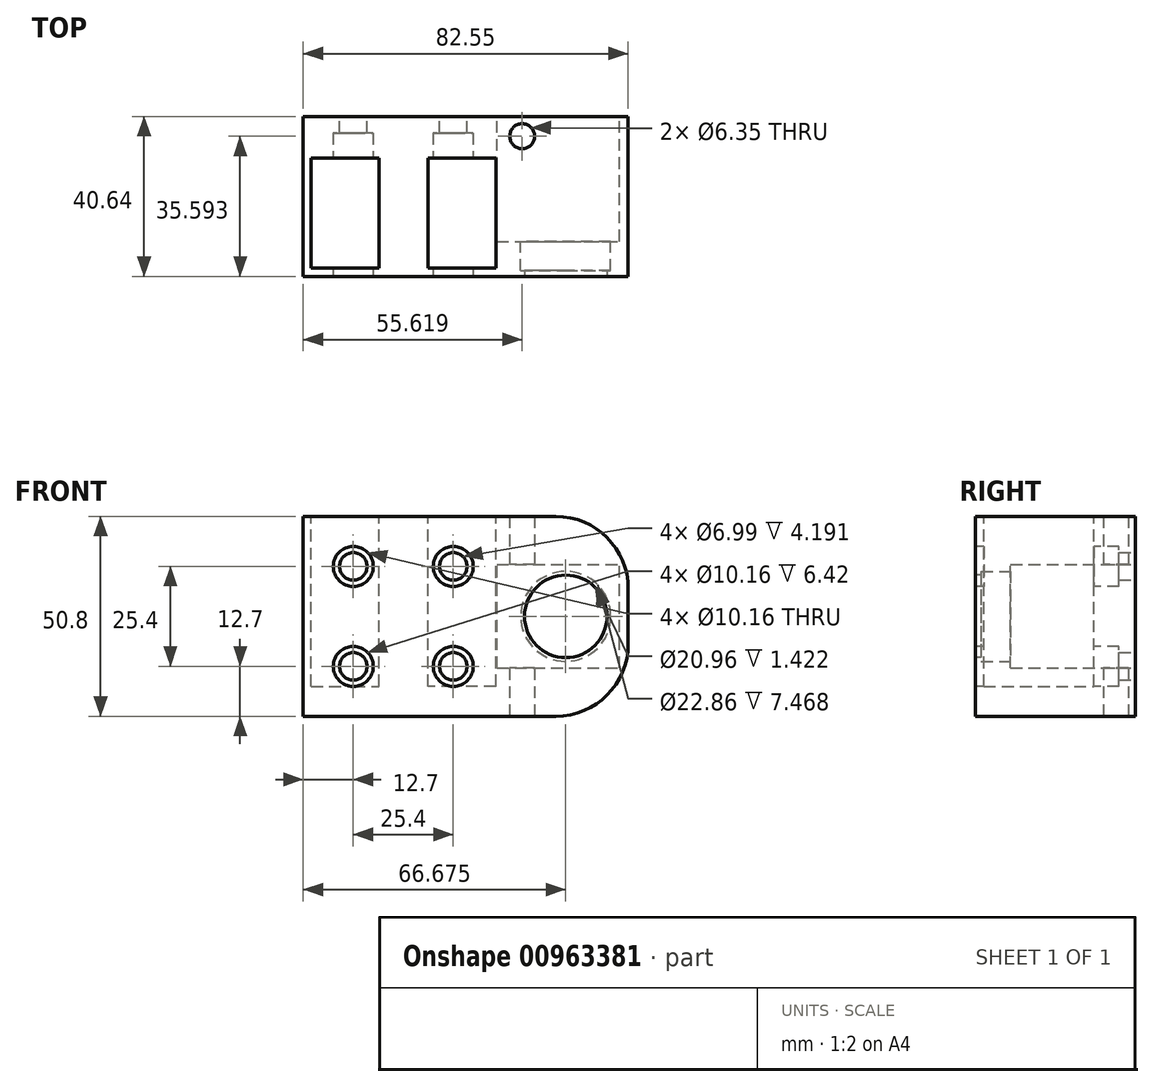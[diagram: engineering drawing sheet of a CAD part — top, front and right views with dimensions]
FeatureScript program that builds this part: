
annotation { "Feature Type Name" : "Feature", "Feature Type Description" : "" }
export const myFeature = defineFeature(function(context is Context, id is Id, definition is map)
    precondition{}
    {
        {
            var Q0;
            Q0=qCreatedBy(makeId("Front.planeOp"),FACE);
            var sketch = newSketch(context, id + "F0", { "sketchPlane" : qUnion([Q0])});
            skLineSegment(sketch, "E0.bottom", {"start": v(-25.4, -25.4) * mm, "end": v(25.4, -25.4) * mm});
            skLineSegment(sketch, "E0.top", {"start": v(-25.4, 25.4) * mm, "end": v(25.4, 25.4) * mm});
            skLineSegment(sketch, "E0.left", {"start": v(-25.4, -25.4) * mm, "end": v(-25.4, 25.4) * mm});
            skLineSegment(sketch, "E0.right", {"start": v(25.4, -25.4) * mm, "end": v(25.4, 25.4) * mm});
            skPoint(sketch, "E0.middle", {"position": v(0, 0) * mm});
            skCircle(sketch, "E1", {"center": v(-12.7, 12.7) * mm, "radius": 3.5 * mm});
            skCircle(sketch, "E2", {"center": v(12.7, 12.7) * mm, "radius": 3.5 * mm});
            skCircle(sketch, "E3", {"center": v(-12.7, -12.7) * mm, "radius": 3.5 * mm});
            skCircle(sketch, "E4", {"center": v(12.7, -12.7) * mm, "radius": 3.5 * mm});
            skSolve(sketch);
        }
        {
            var Q0;
            Q0 = qSketchRegion(id + "F0", true);
            extrude(context, id + "F1", {"entities" : qUnion([Q0]), "depth" : 38.1 * mm, "offsetDistance" : 25.4 * mm});
        }
        {
            var Q0;
            Q0=makeQuery(id+"F1.opExtrude","SWEPT_FACE",FACE,{"disambiguationData":[OSD([sQuery(id+"F0.wireOp",EDGE,"E0.top")])]});
            var sketch = newSketch(context, id + "F2", { "sketchPlane" : qUnion([Q0])});
            skLineSegment(sketch, "E5.bottom", {"start": v(23.52, -36.01) * mm, "end": v(6.25, -36.01) * mm});
            skLineSegment(sketch, "E5.top", {"start": v(23.52, -8.07) * mm, "end": v(6.25, -8.07) * mm});
            skLineSegment(sketch, "E5.left", {"start": v(23.52, -36.01) * mm, "end": v(23.52, -8.07) * mm});
            skLineSegment(sketch, "E5.right", {"start": v(6.25, -36.01) * mm, "end": v(6.25, -8.07) * mm});
            skPoint(sketch, "E5.middle", {"position": v(14.89, -22.04) * mm});
            skLineSegment(sketch, "E6.bottom", {"start": v(-23.4, -36.01) * mm, "end": v(-6.12, -36.01) * mm});
            skLineSegment(sketch, "E6.top", {"start": v(-23.4, -8.07) * mm, "end": v(-6.12, -8.07) * mm});
            skLineSegment(sketch, "E6.left", {"start": v(-23.4, -36.01) * mm, "end": v(-23.4, -8.07) * mm});
            skLineSegment(sketch, "E6.right", {"start": v(-6.12, -36.01) * mm, "end": v(-6.12, -8.07) * mm});
            skPoint(sketch, "E6.middle", {"position": v(-14.76, -22.04) * mm});
            skSolve(sketch);
        }
        {
            var Q0;
            Q0 = qSketchRegion(id + "F2", true);
            extrude(context, id + "F3", {"entities" : qUnion([Q0]), "operationType" : NewBodyOperationType.REMOVE, "oppositeDirection" : true, "depth" : 43.18 * mm, "offsetDistance" : 25.4 * mm});
        }
        {
            var Q0;
            Q0=makeQuery(id+"F1.opExtrude","CAP_FACE",FACE,{"disambiguationData":[OSD([sQuery(id+"F0.wireOp",EDGE,"E0.bottom"),sQuery(id+"F0.wireOp",EDGE,"E0.top"),sQuery(id+"F0.wireOp",EDGE,"E0.left"),sQuery(id+"F0.wireOp",EDGE,"E0.right"),sQuery(id+"F0.wireOp",EDGE,"E1"),sQuery(id+"F0.wireOp",EDGE,"E2"),sQuery(id+"F0.wireOp",EDGE,"E3"),sQuery(id+"F0.wireOp",EDGE,"E4")])],"isStart":false});
            var sketch = newSketch(context, id + "F4", { "sketchPlane" : qUnion([Q0])});
            skCircle(sketch, "E7", {"center": v(-12.7, 12.7) * mm, "radius": 5.08 * mm});
            skCircle(sketch, "E8", {"center": v(12.7, 12.7) * mm, "radius": 5.08 * mm});
            skCircle(sketch, "E9", {"center": v(-12.7, -12.7) * mm, "radius": 5.08 * mm});
            skCircle(sketch, "E10", {"center": v(12.7, -12.7) * mm, "radius": 5.08 * mm});
            skSolve(sketch);
        }
        {
            var Q0;
            Q0 = qSketchRegion(id + "F4", true);
            extrude(context, id + "F5", {"entities" : qUnion([Q0]), "operationType" : NewBodyOperationType.REMOVE, "oppositeDirection" : true, "depth" : 36.45 * mm, "offsetDistance" : 25.4 * mm});
        }
        {
            var Q0;
            Q0=makeQuery(id+"F1.opExtrude","CAP_FACE",FACE,{"disambiguationData":[OSD([sQuery(id+"F0.wireOp",EDGE,"E0.bottom"),sQuery(id+"F0.wireOp",EDGE,"E0.top"),sQuery(id+"F0.wireOp",EDGE,"E0.left"),sQuery(id+"F0.wireOp",EDGE,"E0.right"),sQuery(id+"F0.wireOp",EDGE,"E1"),sQuery(id+"F0.wireOp",EDGE,"E2"),sQuery(id+"F0.wireOp",EDGE,"E3"),sQuery(id+"F0.wireOp",EDGE,"E4")])],"isStart":true});
            extrude(context, id + "F6", {"entities" : qUnion([Q0]), "operationType" : NewBodyOperationType.ADD, "depth" : 2.54 * mm, "offsetDistance" : 25.4 * mm});
        }
        {
            var Q0;
            {var subQ0=sQuery(id+"F0.wireOp",EDGE,"E0.right");Q0=makeQuery(id+"F6.boolean.opBoolean","MERGE",FACE,{"derivedFrom":[makeQuery(id+"F1.opExtrude","SWEPT_FACE",FACE,{"disambiguationData":[OSD([subQ0])]}),makeQuery(id+"F6.opExtrude","SWEPT_FACE",FACE,{"disambiguationData":[OSD([subQ0])]})]});}
            extrude(context, id + "F7", {"entities" : qUnion([Q0]), "operationType" : NewBodyOperationType.ADD, "depth" : 31.75 * mm, "offsetDistance" : 25.4 * mm});
        }
        {
            var Q0;
            {var subQ0=sQuery(id+"F0.wireOp",EDGE,"E0.right");Q0=makeQuery(id+"F7.boolean.opBoolean","MERGE",FACE,{"derivedFrom":[makeQuery(id+"F1.opExtrude","CAP_FACE",FACE,{"disambiguationData":[OSD([sQuery(id+"F0.wireOp",EDGE,"E0.bottom"),sQuery(id+"F0.wireOp",EDGE,"E0.top"),sQuery(id+"F0.wireOp",EDGE,"E0.left"),subQ0,sQuery(id+"F0.wireOp",EDGE,"E1"),sQuery(id+"F0.wireOp",EDGE,"E2"),sQuery(id+"F0.wireOp",EDGE,"E3"),sQuery(id+"F0.wireOp",EDGE,"E4")])],"isStart":false}),makeQuery(id+"F7.opExtrude","SWEPT_FACE",FACE,{"disambiguationData":[OSD([subQ0]),TDD([makeQuery(id+"F1.opExtrude","CAP_EDGE",EDGE,{"disambiguationData":[OSD([subQ0])],"isStart":false})])]})]});}
            var sketch = newSketch(context, id + "F8", { "sketchPlane" : qUnion([Q0])});
            skCircle(sketch, "E11", {"center": v(41.27, 0) * mm, "radius": 10.48 * mm});
            skSolve(sketch);
        }
        {
            var Q0;
            {var subQ0=sQuery(id+"F0.wireOp",EDGE,"E0.right");Q0=makeQuery(id+"F7.boolean.opBoolean","MERGE",FACE,{"derivedFrom":[makeQuery(id+"F6.opExtrude","CAP_FACE",FACE,{"disambiguationData":[OSD([sQuery(id+"F0.wireOp",EDGE,"E0.bottom"),sQuery(id+"F0.wireOp",EDGE,"E0.top"),sQuery(id+"F0.wireOp",EDGE,"E0.left"),subQ0,sQuery(id+"F0.wireOp",EDGE,"E1"),sQuery(id+"F0.wireOp",EDGE,"E2"),sQuery(id+"F0.wireOp",EDGE,"E3"),sQuery(id+"F0.wireOp",EDGE,"E4")])],"isStart":false}),makeQuery(id+"F7.opExtrude","SWEPT_FACE",FACE,{"disambiguationData":[OSD([subQ0]),TDD([makeQuery(id+"F6.opExtrude","CAP_EDGE",EDGE,{"disambiguationData":[OSD([subQ0])],"isStart":false})])]})]});}
            var sketch = newSketch(context, id + "F9", { "sketchPlane" : qUnion([Q0])});
            skLineSegment(sketch, "E12.bottom", {"start": v(-23.77, -23.32) * mm, "end": v(-54.91, -23.32) * mm});
            skLineSegment(sketch, "E12.top", {"start": v(-23.77, 23.32) * mm, "end": v(-54.91, 23.32) * mm});
            skLineSegment(sketch, "E12.left", {"start": v(-23.77, -23.32) * mm, "end": v(-23.77, 23.32) * mm});
            skLineSegment(sketch, "E12.right", {"start": v(-54.91, -23.32) * mm, "end": v(-54.91, 23.32) * mm});
            skPoint(sketch, "E12.middle", {"position": v(-39.34, 0) * mm});
            skSolve(sketch);
        }
        {
            var Q0;
            Q0 = qSketchRegion(id + "F9", true);
            extrude(context, id + "F10", {"entities" : qUnion([Q0]), "operationType" : NewBodyOperationType.REMOVE, "oppositeDirection" : true, "depth" : 31.75 * mm, "offsetDistance" : 25.4 * mm});
        }
        {
            var Q0;
            Q0 = qSketchRegion(id + "F8", true);
            extrude(context, id + "F11", {"entities" : qUnion([Q0]), "operationType" : NewBodyOperationType.REMOVE, "oppositeDirection" : true, "depth" : 25.4 * mm, "offsetDistance" : 25.4 * mm});
        }
        {
            var Q0;
            Q0=makeQuery(id+"F10.boolean.opBoolean","COPY",FACE,{"derivedFrom":makeQuery(id+"F10.opExtrude","CAP_FACE",FACE,{"disambiguationData":[OSD([sQuery(id+"F9.wireOp",EDGE,"E12.bottom"),sQuery(id+"F9.wireOp",EDGE,"E12.top"),sQuery(id+"F9.wireOp",EDGE,"E12.left"),sQuery(id+"F9.wireOp",EDGE,"E12.right")])],"isStart":false})});
            var sketch = newSketch(context, id + "F12", { "sketchPlane" : qUnion([Q0])});
            skCircle(sketch, "E13", {"center": v(-41.27, 0) * mm, "radius": 11.43 * mm});
            skSolve(sketch);
        }
        {
            var Q0;
            Q0 = qSketchRegion(id + "F12", true);
            extrude(context, id + "F13", {"entities" : qUnion([Q0]), "operationType" : NewBodyOperationType.REMOVE, "oppositeDirection" : true, "depth" : 7.47 * mm, "offsetDistance" : 25.4 * mm});
        }
        {
            var Q0;
            Q0=makeQuery(id+"F10.boolean.opBoolean","COPY",FACE,{"derivedFrom":makeQuery(id+"F10.opExtrude","SWEPT_FACE",FACE,{"disambiguationData":[OSD([sQuery(id+"F9.wireOp",EDGE,"E12.top")])]})});
            extrude(context, id + "F14", {"entities" : qUnion([Q0]), "operationType" : NewBodyOperationType.ADD, "depth" : 10.16 * mm, "offsetDistance" : 25.4 * mm});
        }
        {
            var Q0;
            Q0=makeQuery(id+"F10.boolean.opBoolean","COPY",FACE,{"derivedFrom":makeQuery(id+"F10.opExtrude","SWEPT_FACE",FACE,{"disambiguationData":[OSD([sQuery(id+"F9.wireOp",EDGE,"E12.bottom")])]})});
            extrude(context, id + "F15", {"entities" : qUnion([Q0]), "operationType" : NewBodyOperationType.ADD, "depth" : 10.16 * mm, "offsetDistance" : 25.4 * mm});
        }
        {
            var Q0;
            Q0=makeQuery(id+"F7.opExtrude","CAP_EDGE",EDGE,{"disambiguationData":[OSD([sQuery(id+"F0.wireOp",EDGE,"E0.top"),sQuery(id+"F0.wireOp",EDGE,"E0.right")])],"isStart":false});
            var Q1;
            Q1=makeQuery(id+"F7.opExtrude","CAP_EDGE",EDGE,{"disambiguationData":[OSD([sQuery(id+"F0.wireOp",EDGE,"E0.bottom"),sQuery(id+"F0.wireOp",EDGE,"E0.right")])],"isStart":false});
            fillet(context, id + "F16", {"entities" : qUnion([Q0, Q1]), "radius" : 18.4 * mm, "tangentPropagation" : true, "allowEdgeOverflow" : false});
        }
        {
            var Q0;
            Q0=makeQuery(id+"F14.opExtrude","CAP_FACE",FACE,{"disambiguationData":[OSD([sQuery(id+"F9.wireOp",EDGE,"E12.top")])],"isStart":false});
            var sketch = newSketch(context, id + "F17", { "sketchPlane" : qUnion([Q0])});
            skCircle(sketch, "E14", {"center": v(30.22, 2.5) * mm, "radius": 3.18 * mm});
            skSolve(sketch);
        }
        {
            var Q0;
            Q0 = qSketchRegion(id + "F17", true);
            extrude(context, id + "F18", {"entities" : qUnion([Q0]), "operationType" : NewBodyOperationType.REMOVE, "endBound" : BoundingType.SYMMETRIC, "oppositeDirection" : true, "depth" : 115.82 * mm, "offsetDistance" : 25.4 * mm});
        }
    });
